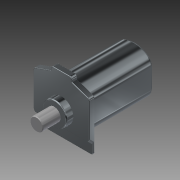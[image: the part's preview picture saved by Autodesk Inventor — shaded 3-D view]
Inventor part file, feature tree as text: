
AUTODESK INVENTOR PART (.ipt)
format: ipt  version: 2018 (Build 220112000, 112)  size: 273,408 bytes
history: native  units: mm
features: fillet x8, extrude x7, sketch x6, chamfer x2
ambient origin geometry x8: Origin, YZ Plane, XZ Plane, XY Plane, X Axis, Y Axis, Z Axis, Center Point
bodies: Solid1 (feature_tree)
feature tree (23):
  extrude  "Extrusion1"  Depth=55.3mm TaperAngle=0.0deg
  sketch  "Sketch2"  dims[d4=53.2mm d5=11.0mm d6=55.3mm d7=0.0mm d8=2.0mm]
  extrude  "Extrusion2"  Depth=2.0mm
  fillet  "Fillet2"  Radius=55.3mm
  fillet  "Fillet1"  Radius=2.0mm
  extrude  "Extrusion3"  Depth=12.9mm
  fillet  "Fillet3"  Radius=6.4mm
  extrude  "Extrusion4"  Depth=2.0mm
  extrude  "Extrusion5"  Depth=1.5mm TaperAngle=0.0deg
  chamfer  "Chamfer1"  Distance=4.5mm
  fillet  "Fillet4"  Radius=2.0mm
  fillet  "Fillet5"  Radius=2.0mm
  fillet  "Fillet6"  Radius=0.5mm
  fillet  "Fillet7"  Radius=45.0mm
  extrude  "Extrusion6"  Depth=2.0mm
  extrude  "Extrusion7"  Depth=2.0mm
  fillet  "Fillet8"  Radius=19.3mm
  chamfer  "Chamfer2"  Distance=5.7mm
  sketch  "Sketch1"  dims[d0=36.0mm d1=55.3mm d2=0.0mm]
  sketch  "Sketch3"  dims[d9=8.0mm d10=12.9mm d11=6.4mm d12=0.0mm]
  sketch  "Sketch4"  dims[d13=0.9mm d15=2.0mm]
  sketch  "Sketch5"  dims[d16=2.0mm d17=1.5mm d18=0.0mm d19=4.5mm d20=0.0mm]
  sketch  "Sketch6"  dims[d21=3.0mm d22=2.0mm d23=45.0deg d24=2.0mm d25=2.0mm d26=0.5mm d28=45.0mm d29=17.0mm d30=2.0mm d31=19.3mm d32=5.7mm d33=0.0mm d34=10.5mm d35=14.3mm d36=0.0mm d37=1.0mm d38=0.5mm d39=2.0mm d40=45.0deg]
